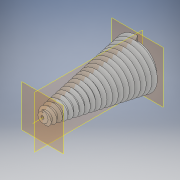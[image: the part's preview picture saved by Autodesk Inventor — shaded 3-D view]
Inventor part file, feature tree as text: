
AUTODESK INVENTOR PART (.ipt)
format: ipt  version: 2018 (Build 220112000, 112)  size: 565,760 bytes
history: native  units: in
note: dims shown in document units (in); Inventor stores cm internally (conversion verified against a paired STEP export)
features: sketch x4, plane x1, loft x1, hole x1, other x1, helix x1, extrude x1, projected_geometry x1
ambient origin geometry x8: Origin, YZ Plane, XZ Plane, XY Plane, X Axis, Y Axis, Z Axis, Center Point
bodies: Solid1 (feature_tree)
feature tree (11):
  sketch  "Sketch1"  dims[d0=2.0in d2=5.0in]
  plane  "Work Plane1"
  loft  "Loft1"
  hole  "Hole1"  [1 undecoded]
  other  "Work Axis2"
  helix  "Coil2"  [1 undecoded]
  extrude  "Extrusion1"  Depth=0.25in
  sketch  "Sketch2"  dims[d3=0.5in d5=0.0in d6=90.0deg d7=0.0in d8=90.0deg]
  sketch  "Sketch6"  dims[d9=1.0in d10=1.0in]
  projected_geometry  "Projected Loop1"
  sketch  "Sketch7"  dims[d11=0.16in d12=0.75in d13=0.375in d14=0.25in d15=0.5635in d16=1.0in d17=0.8108in d29=0.25in d30=0.275in d31=0.25in d32=1.0in d33=7.874in d34=-0.0687in d35=90.0deg d36=90.0deg d37=0.0in d38=0.0in d39=1.0in d40=0.0in]
note: 2 required parameter values undecoded (feature->parameter linkage not recoverable at this tier; creation-order binding heuristic only, values carry confidence <= 0.55)
